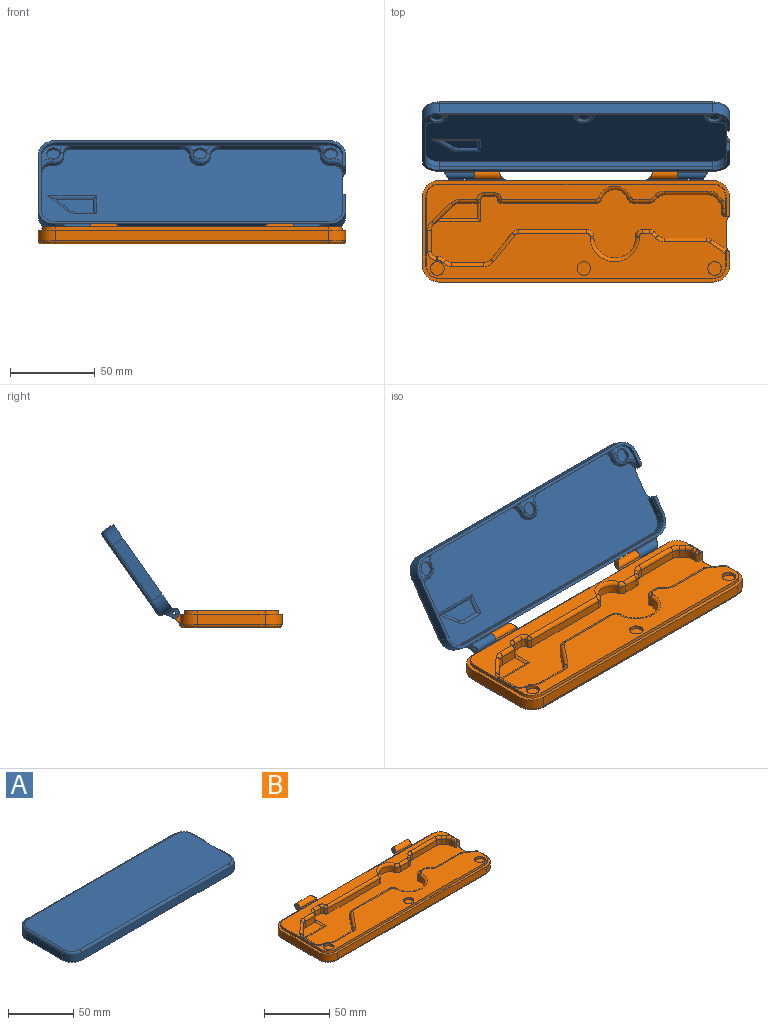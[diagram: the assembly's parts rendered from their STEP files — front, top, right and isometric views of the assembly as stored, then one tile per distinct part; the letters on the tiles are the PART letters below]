
ASSEMBLY  parts=2 mates=1
PART A: 95 faces, bbox 184.8x68.7x11.5 mm
  f0: plane 178.99x56mm, normal (0,0,-1), area 9153.4mm2, adj f1,f2,f3,f4,f5,f6,f7,f8
  f1: plane 64.52x4mm, normal (0,1,0), area 225.4mm2, adj f0,f23,f30,f55,f73,f78
  f2: plane 73.87x4mm, normal (0,1,0), area 262.8mm2, adj f0,f27,f32,f55,f76,f81
  f3: plane 11.31x4mm, normal (-1,0,0), area 45.3mm2, adj f0,f6,f8,f49
  f4: plane 35.81x4mm, normal (1,0,0), area 126.8mm2, adj f0,f7,f35,f53,f79
  f5: plane 160.97x4mm, normal (0,-1,0), area 643.9mm2, adj f0,f6,f7,f51
  f6: cylinder r=8mm len=8mm, axis (0,0,-1), area 50.3mm2, adj f0,f3,f5,f50
  f7: cylinder r=8mm len=8mm, axis (0,0,-1), area 50.2mm2, adj f0,f4,f5,f52
  f8: plane 6x2mm, normal (0,-1,0), area 11.7mm2, adj f0,f3,f9,f20,f49
  f9: plane 11.31x7mm, normal (1,0,0), area 79.2mm2, adj f8,f10,f20,f37,f82
  f10: cylinder r=10mm len=10mm, axis (0,0,-1), area 110mm2, adj f9,f11,f20,f83
  f11: plane 160.97x7.99mm, normal (0,1,0), area 971.9mm2, adj f10,f12,f20,f43,f48,f58,f59,f71
  f12: cylinder r=10mm len=10mm, axis (0,0,-1), area 109.9mm2, adj f11,f13,f20,f89
  f13: plane 40x7mm, normal (-1,0,0), area 280mm2, adj f12,f14,f20,f90
  f14: cylinder r=10mm len=10.01mm, axis (0,0,-1), area 110mm2, adj f13,f15,f20,f91
  f15: plane 161x7mm, normal (0,-1,0), area 1127mm2, adj f14,f16,f20,f92
  f16: cylinder r=10mm len=10mm, axis (0,0,-1), area 110mm2, adj f15,f17,f20,f93
  f17: plane 7.89x7mm, normal (1,0,0), area 55.3mm2, adj f16,f18,f20,f38,f94
  f18: plane 6x2mm, normal (0.56,0.83,0), area 14.1mm2, adj f0,f17,f20,f26,f57
  f19: plane 177x56.26mm, normal (0,0,1), area 9897.2mm2, adj f21,f82,f83,f84,f85,f86,f87,f88
  f20: plane 181x60mm, normal (0,0,-1), area 746.7mm2, adj f8,f9,f10,f11,f12,f13,f14,f15
  f21: plane 12.79x3mm, normal (1,0,0), area 38.4mm2, adj f0,f19,f37,f38
  f22: cylinder r=6mm len=6.78mm, axis (0,0,-1), area 22mm2, adj f0,f23,f26,f74
  f23: cylinder r=4.61mm len=5.22mm, axis (0,0,-1), area 15.7mm2, adj f0,f1,f22,f73
  f24: plane 12.6x12.2mm, normal (0,0,-1), area 46.1mm2, adj f25,f55,f56,f57,f73,f75
  f25: cylinder r=4mm len=8mm, axis (0,0,-1), area 50.3mm2, adj f24,f64,f74
  f26: cylinder r=5.34mm len=6.03mm, axis (0,0,-1), area 20.6mm2, adj f0,f18,f22,f57,f75
  f27: cylinder r=6mm len=6mm, axis (0,0,-1), area 18.8mm2, adj f0,f2,f31,f76
  f28: plane 13.42x6mm, normal (0,0,-1), area 32.8mm2, adj f29,f55,f76,f78
  f29: cylinder r=4mm len=8mm, axis (0,0,-1), area 50.3mm2, adj f28,f63,f77
  f30: cylinder r=6mm len=6mm, axis (0,0,-1), area 18.8mm2, adj f0,f1,f31,f78
  f31: cylinder r=6mm len=12mm, axis (0,0,-1), area 37.7mm2, adj f0,f27,f30,f77
  f32: cylinder r=4.61mm len=5.21mm, axis (0,0,-1), area 15.7mm2, adj f0,f2,f34,f81
  f33: plane 12.59x12.2mm, normal (0,0,-1), area 46mm2, adj f36,f53,f54,f55,f79,f81
  f34: cylinder r=6mm len=6.79mm, axis (0,0,-1), area 22mm2, adj f0,f32,f35,f80
  f35: cylinder r=5.32mm len=6.02mm, axis (0,0,-1), area 18.1mm2, adj f0,f4,f34,f79
  f36: cylinder r=4mm len=8mm, axis (0,0,-1), area 50.3mm2, adj f33,f62,f80
  f37: cylinder r=5mm len=4mm, axis (0,0,-1), area 12.7mm2, adj f0,f9,f21,f82
  f38: cylinder r=5mm len=4mm, axis (0,0,-1), area 12.7mm2, adj f0,f17,f21,f94
  f39: cylinder r=3mm len=17.75mm, axis (-1,0,0), area 199.5mm2, adj f40,f42,f43,f59,f61
  f40: cylinder r=5.81mm len=18.4mm, axis (-1,0,0), area 99.9mm2, adj f39,f43,f59,f85,f86
  f41: cylinder r=1mm len=15.67mm, axis (-1,0,0), area 96.1mm2, adj f43,f59
  f42: plane 5.2x1.5mm, normal (1,0,0), area 5.5mm2, adj f39,f59
  f43: plane 10.49x6.5mm, normal (-1,0,0), area 34.4mm2, adj f11,f39,f40,f41,f61,f72,f86
  f44: cylinder r=3mm len=17.75mm, axis (1,0,0), area 199.5mm2, adj f45,f47,f48,f58,f60
  f45: cylinder r=5.81mm len=18.4mm, axis (1,0,0), area 99.9mm2, adj f44,f48,f58,f86,f87
  f46: cylinder r=1mm len=15.67mm, axis (1,0,0), area 96.1mm2, adj f48,f58
  f47: plane 5.2x1.5mm, normal (-1,0,0), area 5.5mm2, adj f44,f58
  f48: plane 10.49x6.5mm, normal (1,0,0), area 34.4mm2, adj f11,f44,f45,f46,f60,f71,f86
  f49: plane 11.31x2mm, normal (-0.99,0,-0.15), area 22.9mm2, adj f3,f8,f20,f50
  f50: cone r=8.3mm half-angle=8.5deg, axis (0,0,-1), area 25.9mm2, adj f6,f20,f49,f51
  f51: plane 160.97x2mm, normal (0,-0.99,-0.15), area 325.5mm2, adj f5,f20,f50,f52
  f52: cone r=8.3mm half-angle=8.5deg, axis (0,0,-1), area 25.9mm2, adj f7,f20,f51,f53
  f53: plane 40x2mm, normal (0.99,0,-0.15), area 80.9mm2, adj f4,f20,f33,f52,f54
  f54: cone r=8.3mm half-angle=8.5deg, axis (0,0,-1), area 25.9mm2, adj f20,f33,f53,f55
  f55: plane 161x2mm, normal (0,0.99,-0.15), area 325.6mm2, adj f1,f2,f20,f24,f28,f33,f54,f56
  f56: cone r=8.3mm half-angle=8.5deg, axis (0,0,-1), area 25.9mm2, adj f20,f24,f55,f57
  f57: plane 9.24x4mm, normal (-0.99,0,-0.15), area 21mm2, adj f18,f20,f24,f26,f56,f75
  f58: cylinder r=5mm len=9.5mm, axis (0,0,-1), area 47.6mm2, adj f11,f44,f45,f46,f47,f60,f71,f87
  f59: cylinder r=5mm len=9.5mm, axis (0,0,1), area 47.6mm2, adj f11,f39,f40,f41,f42,f61,f72,f85
  f60: cylinder r=5mm len=17.81mm, axis (-1,0,0), area 3.1mm2, adj f44,f48,f58,f71
  f61: cylinder r=5mm len=17.81mm, axis (1,0,0), area 3.1mm2, adj f39,f43,f59,f72
  f62: plane 8x8mm, normal (0,0,-1), area 50.3mm2, adj f36
  f63: plane 8x8mm, normal (0,0,-1), area 50.3mm2, adj f29
  f64: plane 8x8mm, normal (0,0,-1), area 50.3mm2, adj f25
  f65: plane 21.88x8.85mm, normal (0,0,-1), area 151.7mm2, adj f66,f67,f68,f69,f70
  f66: cylinder r=2mm len=12.45mm, axis (1,0,0), area 29.8mm2, adj f0,f65,f67,f68
  f67: cylinder r=2mm len=12.73mm, axis (0,-1,0), area 27.5mm2, adj f0,f65,f66,f69
  f68: torus R=6.94mm, axis (0,0,1), area 11.6mm2, adj f0,f65,f66,f70
  f69: cylinder r=2mm len=28.7mm, axis (-1,0,0), area 65.1mm2, adj f0,f65,f67,f70
  f70: cylinder r=2mm len=12.81mm, axis (0.73,0.69,0), area 34.1mm2, adj f0,f65,f68,f69
  f71: cylinder r=0.26mm len=20mm, axis (-1,0,0), area 14mm2, adj f11,f48,f58,f60
  f72: cylinder r=0.26mm len=20mm, axis (1,0,0), area 14mm2, adj f11,f43,f59,f61
  f73: torus R=6.61mm, axis (0,0,1), area 20.5mm2, adj f1,f23,f24,f74
  f74: torus R=4mm, axis (0,0,1), area 30.4mm2, adj f22,f25,f73,f75
  f75: torus R=7.34mm, axis (0,0,1), area 22.6mm2, adj f24,f26,f57,f74
  f76: torus R=8mm, axis (0,0,1), area 24.3mm2, adj f2,f27,f28,f77
  f77: torus R=4mm, axis (0,0,1), area 52mm2, adj f29,f31,f76,f78
  f78: torus R=8mm, axis (0,0,1), area 24.3mm2, adj f1,f28,f30,f77
  f79: torus R=7.32mm, axis (0,0,1), area 23.9mm2, adj f4,f33,f35,f80
  f80: torus R=4mm, axis (0,0,1), area 30.4mm2, adj f34,f36,f79,f81
  f81: torus R=6.61mm, axis (0,0,1), area 20.5mm2, adj f2,f32,f33,f80
  f82: cylinder r=2mm len=15.31mm, axis (0,-1,0), area 38.2mm2, adj f9,f19,f37,f83
  f83: torus R=8mm, axis (0,0,1), area 45.8mm2, adj f10,f19,f82,f84
  f84: cylinder r=2mm len=2mm, axis (1,0,0), area 1.6mm2, adj f11,f19,f83,f85
  f85: torus R=7mm, axis (0,0,1), area 5.5mm2, adj f19,f40,f59,f84,f86
  f86: cylinder r=2mm len=156.79mm, axis (1,0,0), area 348.9mm2, adj f11,f19,f40,f43,f45,f48,f85,f87
  f87: torus R=7mm, axis (0,0,1), area 5.5mm2, adj f19,f45,f58,f86,f88
  f88: cylinder r=2mm len=2mm, axis (1,0,0), area 1.5mm2, adj f11,f19,f87,f89
  f89: torus R=8mm, axis (0,0,1), area 45.7mm2, adj f12,f19,f88,f90
  f90: cylinder r=2mm len=40mm, axis (0,1,0), area 125.7mm2, adj f13,f19,f89,f91
  f91: torus R=8mm, axis (0,0,1), area 45.8mm2, adj f14,f19,f90,f92
  f92: cylinder r=2mm len=161mm, axis (-1,0,0), area 505.8mm2, adj f15,f19,f91,f93
  f93: torus R=8mm, axis (0,0,1), area 45.8mm2, adj f16,f19,f92,f94
  f94: cylinder r=2mm len=11.89mm, axis (0,-1,0), area 27.5mm2, adj f17,f19,f38,f93
PART B: 159 faces, bbox 182.7x67.4x11.6 mm
  f0: plane 12.79x3mm, normal (1,0,0), area 38.4mm2, adj f53,f54,f69,f70
  f1: plane 18.94x4.8mm, normal (0,1,0), area 90.9mm2, adj f40,f41,f54,f127
  f2: plane 10.51x5.8mm, normal (0,-1,0), area 61mm2, adj f3,f50,f68,f118
  f3: cylinder r=2mm len=5.8mm, axis (0,0,-1), area 15.7mm2, adj f2,f4,f54,f117,f144
  f4: plane 4.8x0.11mm, normal (1,0,0), area 0.5mm2, adj f3,f5,f54,f115
  f5: cylinder r=2mm len=4.8mm, axis (0,0,-1), area 15.1mm2, adj f4,f6,f54,f114
  f6: plane 6x4.8mm, normal (0,-1,0), area 28.8mm2, adj f5,f7,f54,f113
  f7: cylinder r=2mm len=4.8mm, axis (0,0,-1), area 15.1mm2, adj f6,f8,f54,f112
  f8: plane 4.8x0.11mm, normal (-1,0,0), area 0.5mm2, adj f7,f9,f54,f111
  f9: cylinder r=2mm len=4.8mm, axis (0,0,-1), area 15.1mm2, adj f8,f10,f54,f109
  f10: plane 55.69x4.8mm, normal (0,-1,0), area 267.3mm2, adj f9,f11,f54,f108
  f11: cylinder r=4mm len=4.8mm, axis (0,0,-1), area 23.6mm2, adj f10,f12,f54,f107
  f12: cylinder r=8mm len=15.09mm, axis (0,0,-1), area 94.5mm2, adj f11,f13,f54,f106
  f13: cylinder r=4mm len=4.8mm, axis (0,0,-1), area 23.6mm2, adj f12,f14,f54,f105
  f14: plane 9.11x4.8mm, normal (0,-1,0), area 43.7mm2, adj f13,f15,f54,f104
  f15: cylinder r=4mm len=4.8mm, axis (0,0,-1), area 15.3mm2, adj f14,f16,f54,f103
  f16: plane 4.8x2.3mm, normal (0.71,-0.7,0), area 15.4mm2, adj f15,f17,f54,f102
  f17: cylinder r=5mm len=4.8mm, axis (0,0,-1), area 19.1mm2, adj f16,f18,f54,f101
  f18: plane 26.44x4.8mm, normal (0,-1,0), area 126.9mm2, adj f17,f19,f54,f100
  f19: cylinder r=5mm len=4.8mm, axis (0,0,-1), area 19.6mm2, adj f18,f20,f54,f99
  f20: plane 4.8x2.83mm, normal (-0.73,-0.69,0), area 18.6mm2, adj f19,f21,f54,f98
  f21: cylinder r=5mm len=4.8mm, axis (0,0,-1), area 18.1mm2, adj f20,f22,f54,f97
  f22: plane 4.8x3.42mm, normal (-1,0,0), area 16.4mm2, adj f21,f23,f54,f96
  f23: cylinder r=1.5mm len=4.8mm, axis (0,0,-1), area 11.3mm2, adj f22,f24,f54,f95
  f24: plane 4.8x3mm, normal (0,-1,0), area 14.4mm2, adj f23,f54,f55,f94
  f25: plane 10.69x7.19mm, normal (0.56,0.83,0), area 61.8mm2, adj f26,f54,f63,f143
  f26: cylinder r=5mm len=4.8mm, axis (0,0,-1), area 14.2mm2, adj f25,f27,f54,f142
  f27: plane 25.12x4.8mm, normal (0,1,0), area 120.6mm2, adj f26,f28,f54,f141
  f28: cylinder r=5mm len=4.8mm, axis (0,0,-1), area 19.1mm2, adj f27,f29,f54,f140
  f29: plane 4.8x2.3mm, normal (0.71,0.7,0), area 15.4mm2, adj f28,f30,f54,f139
  f30: cylinder r=4mm len=4.8mm, axis (0,0,-1), area 15.3mm2, adj f29,f31,f54,f138
  f31: plane 4.8x4.14mm, normal (0,1,0), area 19.9mm2, adj f30,f32,f54,f137
  f32: cylinder r=4mm len=4.8mm, axis (0,0,-1), area 30.2mm2, adj f31,f33,f54,f136
  f33: plane 4.8x0.45mm, normal (-1,0,0), area 2.1mm2, adj f32,f34,f54,f135
  f34: cylinder r=12.28mm len=24.55mm, axis (0,0,-1), area 182.4mm2, adj f33,f35,f54,f134
  f35: plane 4.8x1.2mm, normal (1,0.05,0), area 5.8mm2, adj f34,f36,f54,f133
  f36: cylinder r=4mm len=4.8mm, axis (0,0,-1), area 29.3mm2, adj f35,f37,f54,f132
  f37: plane 40.28x4.8mm, normal (0,1,0), area 193.3mm2, adj f36,f38,f54,f131
  f38: cylinder r=5mm len=4.8mm, axis (0,0,-1), area 21.5mm2, adj f37,f39,f54,f130
  f39: plane 15.75x12.61mm, normal (-0.78,0.62,0), area 96.8mm2, adj f38,f40,f54,f129
  f40: cylinder r=5mm len=4.8mm, axis (0,0,-1), area 21.5mm2, adj f1,f39,f54,f128
  f41: cylinder r=5mm len=4.8mm, axis (0,0,-1), area 19mm2, adj f1,f42,f54,f126
  f42: cylinder r=7mm len=4.98mm, axis (0,0,-1), area 26.6mm2, adj f41,f43,f54,f125
  f43: plane 4.8x0.51mm, normal (0,1,0), area 2.4mm2, adj f42,f44,f54,f124
  f44: cylinder r=3mm len=4.8mm, axis (0,0,-1), area 22.6mm2, adj f43,f45,f54,f123
  f45: plane 12.6x4.8mm, normal (1,0,0), area 60.5mm2, adj f44,f46,f54,f122
  f46: cylinder r=5mm len=4.8mm, axis (0,0,-1), area 19.5mm2, adj f45,f47,f54,f121
  f47: plane 11.49x10.83mm, normal (0.69,-0.73,0), area 87.5mm2, adj f46,f50,f54,f68,f120,f145
  f48: cylinder r=4mm len=8mm, axis (0,0,-1), area 50.3mm2, adj f52,f66
  f49: cylinder r=4mm len=8mm, axis (0,0,-1), area 50.3mm2, adj f52,f65
  f50: cylinder r=5mm len=5.8mm, axis (0,0,-1), area 21.9mm2, adj f2,f47,f68,f119
  f51: cylinder r=4mm len=8mm, axis (0,0,-1), area 50.3mm2, adj f52,f67
  f52: plane 176.6x55.42mm, normal (0,0,1), area 4391.7mm2, adj f48,f49,f51,f81,f82,f83,f84,f85
  f53: plane 177.4x56.46mm, normal (0,0,-1), area 9951mm2, adj f0,f69,f70,f74,f79,f148,f149,f150
  f54: plane 175.7x43mm, normal (0,0,1), area 4048.7mm2, adj f0,f1,f3,f4,f5,f6,f7,f8
  f55: plane 11.31x6.2mm, normal (1,0,0), area 70.2mm2, adj f24,f56,f64,f69,f94,f156
  f56: cylinder r=10mm len=10mm, axis (0,0,-1), area 97.4mm2, adj f55,f57,f64,f157
  f57: plane 160.97x6.99mm, normal (0,1,0), area 821.1mm2, adj f56,f58,f64,f74,f79,f90,f91,f146
  f58: cylinder r=10mm len=10mm, axis (0,0,-1), area 97.3mm2, adj f57,f59,f64,f154
  f59: plane 40x6.2mm, normal (-1,0,0), area 248mm2, adj f58,f60,f64,f153
  f60: cylinder r=10mm len=10.01mm, axis (0,0,-1), area 97.4mm2, adj f59,f61,f64,f152
  f61: plane 161x6.2mm, normal (0,-1,0), area 998.2mm2, adj f60,f62,f64,f151
  f62: cylinder r=10mm len=10mm, axis (0,0,-1), area 97.4mm2, adj f61,f63,f64,f150
  f63: plane 7.9x6.2mm, normal (1,0,0), area 48.9mm2, adj f25,f62,f64,f70,f143,f149
  f64: plane 181x60mm, normal (0,0,1), area 939.4mm2, adj f55,f56,f57,f58,f59,f60,f61,f62
  f65: plane 8x8mm, normal (0,0,1), area 50.3mm2, adj f49
  f66: plane 8x8mm, normal (0,0,1), area 50.3mm2, adj f48
  f67: plane 8x8mm, normal (0,0,1), area 50.3mm2, adj f51
  f68: plane 21.88x8.85mm, normal (0,0,1), area 151.7mm2, adj f2,f47,f50,f144,f145
  f69: cylinder r=5mm len=4mm, axis (0,0,-1), area 12.9mm2, adj f0,f53,f54,f55,f156
  f70: cylinder r=5mm len=4mm, axis (0,0,-1), area 12.9mm2, adj f0,f53,f54,f63,f149
  f71: cylinder r=3mm len=17.75mm, axis (-1,0,0), area 199.5mm2, adj f73,f74,f75,f91,f93
  f72: cylinder r=1mm len=15.67mm, axis (-1,0,0), area 96.1mm2, adj f74,f91
  f73: cylinder r=5.81mm len=18.62mm, axis (-1,0,0), area 100mm2, adj f71,f74,f91,f148
  f74: plane 11.5x8.3mm, normal (1,0,0), area 34.3mm2, adj f53,f57,f71,f72,f73,f93,f147,f148
  f75: plane 5.2x1.5mm, normal (-1,0,0), area 5.5mm2, adj f71,f91
  f76: cylinder r=3mm len=17.75mm, axis (1,0,0), area 199.5mm2, adj f78,f79,f80,f90,f92
  f77: cylinder r=1mm len=15.67mm, axis (1,0,0), area 96.1mm2, adj f79,f90
  f78: cylinder r=5.81mm len=18.62mm, axis (1,0,0), area 100mm2, adj f76,f79,f90,f148
  f79: plane 11.5x8.3mm, normal (-1,0,0), area 34.3mm2, adj f53,f57,f76,f77,f78,f92,f146,f148
  f80: plane 5.2x1.5mm, normal (1,0,0), area 5.5mm2, adj f76,f90
  f81: plane 11.39x2.09mm, normal (1,0,0.1), area 21.7mm2, adj f52,f64,f82,f94
  f82: cone r=7.8mm half-angle=5.7deg, axis (0,0,-1), area 20.8mm2, adj f52,f64,f81,f89
  f83: cone r=7.8mm half-angle=5.7deg, axis (0,0,-1), area 20.7mm2, adj f52,f64,f84,f89
  f84: plane 40x2mm, normal (-1,0,0.1), area 80.4mm2, adj f52,f64,f83,f85
  f85: cone r=7.8mm half-angle=5.7deg, axis (0,0,-1), area 25mm2, adj f52,f64,f84,f86
  f86: plane 161x2mm, normal (0,-1,0.1), area 323.6mm2, adj f52,f64,f85,f87
  f87: cone r=7.8mm half-angle=5.7deg, axis (0,0,-1), area 24.9mm2, adj f52,f64,f86,f88
  f88: plane 9.23x2mm, normal (1,0,0.1), area 17.4mm2, adj f52,f64,f87,f143
  f89: plane 165.92x2.07mm, normal (0,1,0), area 330.2mm2, adj f52,f64,f82,f83
  f90: cylinder r=5mm len=10.49mm, axis (0,0,1), area 47.2mm2, adj f57,f76,f77,f78,f80,f92,f146,f148
  f91: cylinder r=5mm len=10.49mm, axis (0,0,-1), area 47.2mm2, adj f57,f71,f72,f73,f75,f93,f147,f148
  f92: cylinder r=5mm len=18.63mm, axis (-1,0,0), area 22.6mm2, adj f76,f79,f90,f146
  f93: cylinder r=5mm len=18.63mm, axis (1,0,0), area 22.6mm2, adj f71,f74,f91,f147
  f94: cylinder r=2.2mm len=3mm, axis (-1,0,0), area 2.7mm2, adj f24,f52,f55,f64,f81,f95
  f95: bspline ~2.68x2.2mm, area 5.4mm2, adj f23,f94,f96
  f96: cylinder r=2.2mm len=3.42mm, axis (0,1,0), area 11mm2, adj f22,f52,f95,f97
  f97: torus R=7.2mm, axis (0,0,1), area 15.1mm2, adj f21,f52,f96,f98
  f98: cylinder r=2.2mm len=4.33mm, axis (-0.69,0.73,0), area 13.4mm2, adj f20,f52,f97,f99
  f99: torus R=7.2mm, axis (0,0,1), area 16.3mm2, adj f19,f52,f98,f100
  f100: cylinder r=2.2mm len=26.44mm, axis (-1,0,0), area 91.4mm2, adj f18,f52,f99,f101
  f101: torus R=7.2mm, axis (0,0,1), area 15.9mm2, adj f17,f52,f100,f102
  f102: cylinder r=2.2mm len=3.84mm, axis (-0.7,-0.71,0), area 11.1mm2, adj f16,f52,f101,f103
  f103: torus R=1.8mm, axis (0,0,1), area 8.8mm2, adj f15,f52,f102,f104
  f104: cylinder r=2.2mm len=9.11mm, axis (-1,0,0), area 31.5mm2, adj f14,f52,f103,f105
  f105: torus R=1.8mm, axis (0,0,1), area 13.6mm2, adj f13,f52,f104,f106
  f106: torus R=10.2mm, axis (0,0,1), area 74.9mm2, adj f12,f52,f105,f107
  f107: torus R=1.8mm, axis (0,0,1), area 13.6mm2, adj f11,f52,f106,f108
  f108: cylinder r=2.2mm len=55.69mm, axis (-1,0,0), area 192.1mm2, adj f10,f52,f107,f109,f110
  f109: bspline ~2.32x2.13mm, area 6.5mm2, adj f9,f108,f110,f111
  f110: bspline ~1.45x1.45mm, area 0.5mm2, adj f108,f109,f112
  f111: cylinder r=2.2mm len=1.97mm, axis (0,1,0), area 0.1mm2, adj f8,f109,f112
  f112: torus R=4.2mm, axis (0,0,1), area 15.2mm2, adj f7,f52,f110,f111,f113
  f113: cylinder r=2.2mm len=6mm, axis (-1,0,0), area 20.7mm2, adj f6,f52,f112,f114
  f114: torus R=4.2mm, axis (0,0,1), area 15.2mm2, adj f5,f52,f113,f115,f116
  f115: cylinder r=2.2mm len=1.97mm, axis (0,-1,0), area 0.1mm2, adj f4,f114,f117
  f116: bspline ~1.45x1.45mm, area 0.5mm2, adj f114,f117,f118
  f117: bspline ~2.32x2.13mm, area 6.5mm2, adj f3,f115,f116,f118
  f118: cylinder r=2.2mm len=10.51mm, axis (-1,0,0), area 36mm2, adj f2,f52,f116,f117,f119
  f119: torus R=7.2mm, axis (0,0,1), area 15.2mm2, adj f50,f52,f118,f120
  f120: cylinder r=2.2mm len=13mm, axis (-0.73,-0.69,0), area 54.6mm2, adj f47,f52,f119,f121
  f121: torus R=7.2mm, axis (0,0,1), area 16.3mm2, adj f46,f52,f120,f122
  f122: cylinder r=2.2mm len=12.6mm, axis (0,-1,0), area 43.5mm2, adj f45,f52,f121,f123
  f123: torus R=5.2mm, axis (0,0,1), area 20.6mm2, adj f44,f52,f122,f124
  f124: cylinder r=2.2mm len=2.2mm, axis (1,0,0), area 1.8mm2, adj f43,f52,f123,f125
  f125: torus R=4.8mm, axis (0,0,1), area 17mm2, adj f42,f52,f124,f126
  f126: torus R=7.2mm, axis (0,0,1), area 15.9mm2, adj f41,f52,f125,f127
  f127: cylinder r=2.2mm len=18.94mm, axis (1,0,0), area 65.5mm2, adj f1,f52,f126,f128
  f128: torus R=7.2mm, axis (0,0,1), area 18mm2, adj f40,f52,f127,f129
  f129: cylinder r=2.2mm len=17.12mm, axis (0.62,0.78,0), area 69.7mm2, adj f39,f52,f128,f130
  f130: torus R=2.8mm, axis (0,0,1), area 13mm2, adj f38,f52,f129,f131
  f131: cylinder r=2.2mm len=40.28mm, axis (1,0,0), area 139.2mm2, adj f37,f52,f130,f132
  f132: torus R=1.8mm, axis (0,0,1), area 16.9mm2, adj f36,f52,f131,f133
  f133: cylinder r=2.2mm len=2.25mm, axis (0.05,-1,0), area 4.2mm2, adj f35,f52,f132,f134
  f134: torus R=14.48mm, axis (0,0,1), area 139.9mm2, adj f34,f52,f133,f135
  f135: cylinder r=2.2mm len=2.2mm, axis (0,1,0), area 1.5mm2, adj f33,f52,f134,f136
  f136: torus R=1.8mm, axis (0,0,1), area 17.4mm2, adj f32,f52,f135,f137
  f137: cylinder r=2.2mm len=4.14mm, axis (1,0,0), area 14.3mm2, adj f31,f52,f136,f138
  f138: torus R=1.8mm, axis (0,0,1), area 8.8mm2, adj f30,f52,f137,f139
  f139: cylinder r=2.2mm len=3.84mm, axis (0.7,-0.71,0), area 11.1mm2, adj f29,f52,f138,f140
  f140: torus R=7.2mm, axis (0,0,1), area 15.9mm2, adj f28,f52,f139,f141
  f141: cylinder r=2.2mm len=25.12mm, axis (1,0,0), area 86.8mm2, adj f27,f52,f140,f142
  f142: torus R=2.8mm, axis (0,0,1), area 8.6mm2, adj f26,f52,f141,f143
  f143: cylinder r=2.2mm len=11.93mm, axis (0.83,-0.56,0), area 38mm2, adj f25,f52,f63,f64,f88,f142
  f144: cylinder r=2.2mm len=11.92mm, axis (0,-1,0), area 21.8mm2, adj f3,f54,f68,f145
  f145: cylinder r=2.2mm len=25.68mm, axis (-1,0,0), area 51.6mm2, adj f47,f54,f68,f144
  f146: cylinder r=0.1mm len=20mm, axis (-1,0,0), area 5.3mm2, adj f57,f79,f90,f92
  f147: cylinder r=0.1mm len=20mm, axis (1,0,0), area 5.3mm2, adj f57,f74,f91,f93
  f148: cylinder r=2mm len=120mm, axis (-1,0,0), area 272.7mm2, adj f53,f57,f73,f74,f78,f79,f90,f91
  f149: cylinder r=1.8mm len=10.49mm, axis (0,1,0), area 24.3mm2, adj f53,f63,f70,f150
  f150: torus R=8.2mm, axis (0,0,1), area 41.5mm2, adj f53,f62,f149,f151
  f151: cylinder r=1.8mm len=161mm, axis (1,0,0), area 455.2mm2, adj f53,f61,f150,f152
  f152: torus R=8.2mm, axis (0,0,1), area 41.5mm2, adj f53,f60,f151,f153
  f153: cylinder r=1.8mm len=40mm, axis (0,-1,0), area 113.1mm2, adj f53,f59,f152,f154
  f154: torus R=8.2mm, axis (0,0,1), area 41.5mm2, adj f53,f58,f153,f155
  f155: cylinder r=1.8mm len=20.46mm, axis (1,0,0), area 57.9mm2, adj f53,f57,f79,f154
  f156: cylinder r=1.8mm len=13.91mm, axis (0,1,0), area 34mm2, adj f53,f55,f69,f157
  f157: torus R=8.2mm, axis (0,0,1), area 41.5mm2, adj f53,f56,f156,f158
  f158: cylinder r=1.8mm len=20.5mm, axis (1,0,0), area 58mm2, adj f53,f57,f74,f157
PLACE A rot(axis=(-1,0,0),125deg) t=(5.78,45.83,23.7)mm
PLACE B t=(5.78,13.75,-10)mm fixed
MATE revolute A.f39 <-> B.f71  axis (1,0,0) through (-54.22,38.56,-1.5)mm
